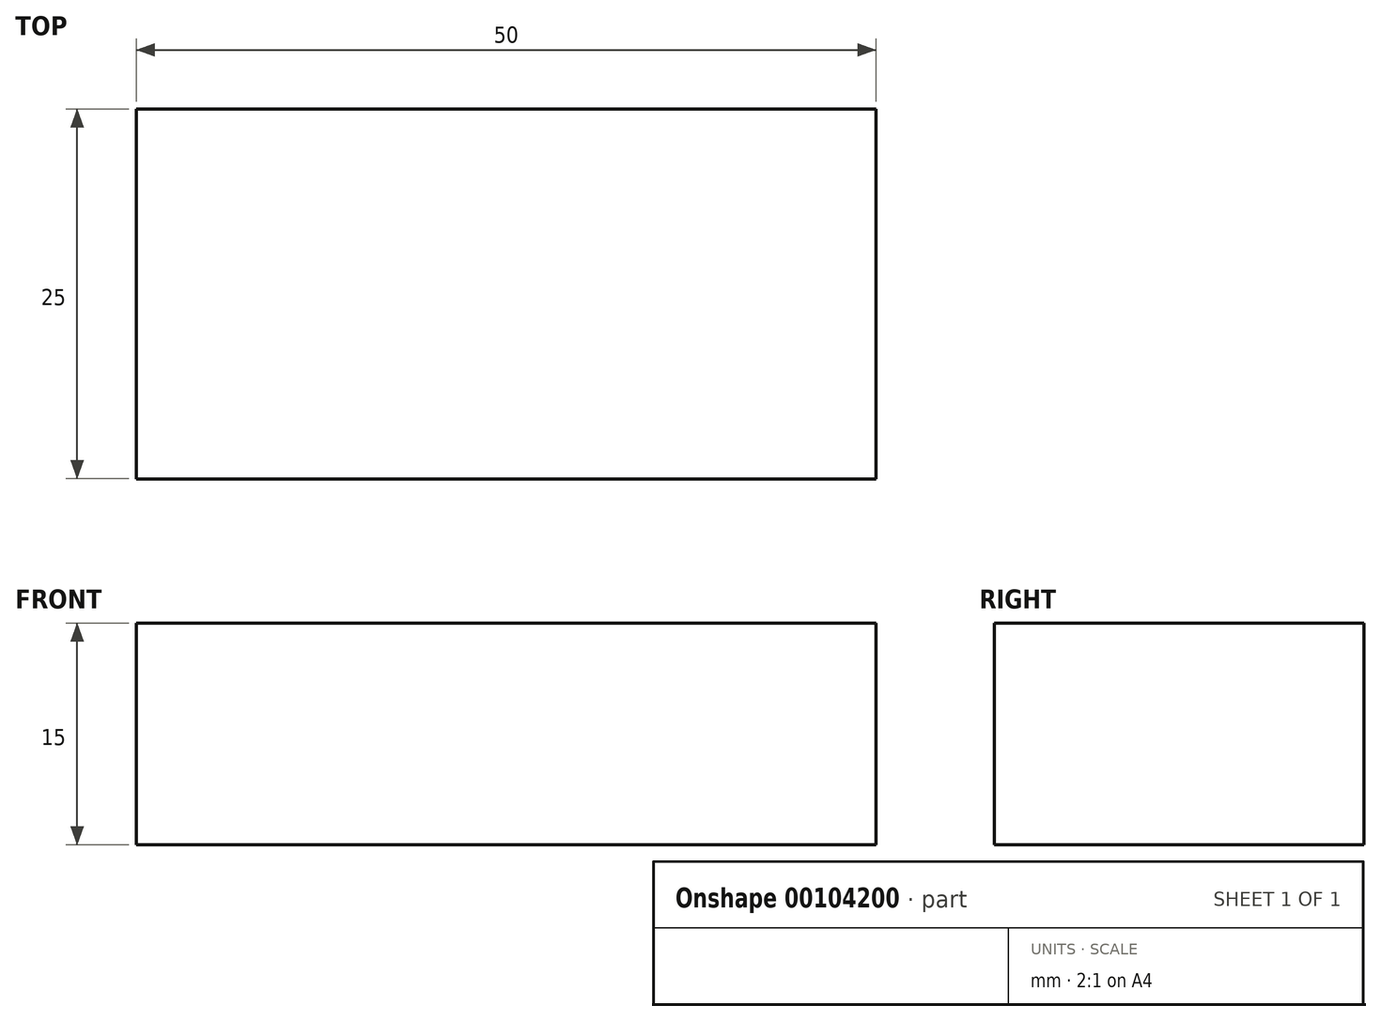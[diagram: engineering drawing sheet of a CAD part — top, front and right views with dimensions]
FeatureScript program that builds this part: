
annotation { "Feature Type Name" : "Feature", "Feature Type Description" : "" }
export const myFeature = defineFeature(function(context is Context, id is Id, definition is map)
    precondition{}
    {
        {
            var Q0;
            Q0=qCreatedBy(makeId("Top.planeOp"),FACE);
            var sketch = newSketch(context, id + "F0", { "sketchPlane" : qUnion([Q0])});
            skLineSegment(sketch, "E0.bottom", {"start": v(-42.74, 11.2) * mm, "end": v(7.26, 11.2) * mm});
            skLineSegment(sketch, "E0.top", {"start": v(-42.74, -13.8) * mm, "end": v(7.26, -13.8) * mm});
            skLineSegment(sketch, "E0.left", {"start": v(-42.74, 11.2) * mm, "end": v(-42.74, -13.8) * mm});
            skLineSegment(sketch, "E0.right", {"start": v(7.26, 11.2) * mm, "end": v(7.26, -13.8) * mm});
            skSolve(sketch);
        }
        {
            var Q0;
            Q0=makeQuery(id+"F0.imprint","IMPRINT",FACE,{"disambiguationData":[TD([[makeQuery(id+"F0.imprint","IMPRINT",EDGE,{"derivedFrom":sQuery(id+"F0.wireOp",EDGE,"E0.bottom")}),-1.0]])]});
            extrude(context, id + "F1", {"entities" : qUnion([Q0]), "depth" : 15 * mm});
        }
    });
